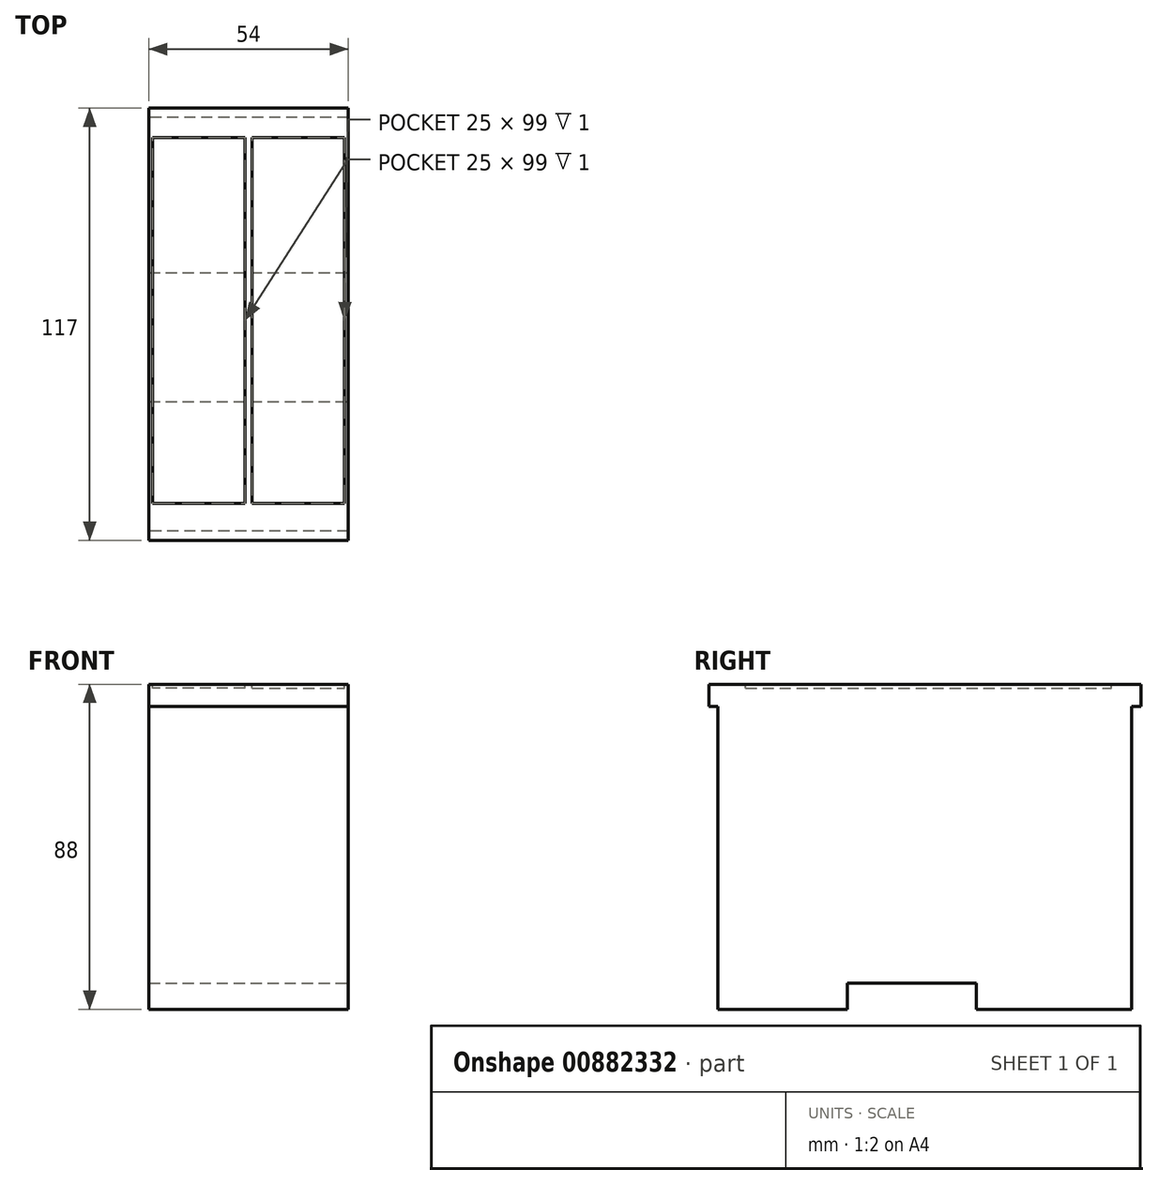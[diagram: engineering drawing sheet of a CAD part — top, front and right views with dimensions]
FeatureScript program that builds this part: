
annotation { "Feature Type Name" : "Feature", "Feature Type Description" : "" }
export const myFeature = defineFeature(function(context is Context, id is Id, definition is map)
    precondition{}
    {
        {
            var Q0;
            Q0=qCreatedBy(makeId("Top.planeOp"),FACE);
            var sketch = newSketch(context, id + "F0", { "sketchPlane" : qUnion([Q0])});
            skLineSegment(sketch, "E0.bottom", {"start": v(0, 58.5) * mm, "end": v(-27, 58.5) * mm});
            skLineSegment(sketch, "E0.top", {"start": v(0, -58.5) * mm, "end": v(-27, -58.5) * mm});
            skLineSegment(sketch, "E0.left", {"start": v(0, 58.5) * mm, "end": v(0, -58.5) * mm});
            skLineSegment(sketch, "E0.right", {"start": v(-27, 58.5) * mm, "end": v(-27, -58.5) * mm});
            skLineSegment(sketch, "E1.bottom", {"start": v(0, 58.5) * mm, "end": v(27, 58.5) * mm});
            skLineSegment(sketch, "E1.top", {"start": v(0, -58.5) * mm, "end": v(27, -58.5) * mm});
            skLineSegment(sketch, "E1.right", {"start": v(27, 58.5) * mm, "end": v(27, -58.5) * mm});
            skLineSegment(sketch, "E2.bottom", {"start": v(1, -48.5) * mm, "end": v(26, -48.5) * mm});
            skLineSegment(sketch, "E2.top", {"start": v(1, 50.5) * mm, "end": v(26, 50.5) * mm});
            skLineSegment(sketch, "E2.left", {"start": v(1, -48.5) * mm, "end": v(1, 50.5) * mm});
            skLineSegment(sketch, "E2.right", {"start": v(26, -48.5) * mm, "end": v(26, 50.5) * mm});
            skPoint(sketch, "E3", {"position": v(13.5, -48.5) * mm});
            skPoint(sketch, "E4", {"position": v(13.5, -58.5) * mm});
            skLineSegment(sketch, "E5.MirrorCS", {"start": v(-1, 50.5) * mm, "end": v(-26, 50.5) * mm});
            skLineSegment(sketch, "E6.MirrorCS", {"start": v(-1, -48.5) * mm, "end": v(-1, 50.5) * mm});
            skLineSegment(sketch, "E7.MirrorCS", {"start": v(-1, -48.5) * mm, "end": v(-26, -48.5) * mm});
            skLineSegment(sketch, "E8.MirrorCS", {"start": v(-26, -48.5) * mm, "end": v(-26, 50.5) * mm});
            skSolve(sketch);
        }
        {
            var Q0;
            Q0 = qSketchRegion(id + "F0", true);
            var Q1;
            Q1=makeQuery(id+"F0.imprint","IMPRINT",FACE,{"disambiguationData":[TD([[makeQuery(id+"F0.imprint","IMPRINT",EDGE,{"derivedFrom":sQuery(id+"F0.wireOp",EDGE,"E5.MirrorCS")}),1.0]])]});
            var Q2;
            Q2=makeQuery(id+"F0.imprint","IMPRINT",FACE,{"disambiguationData":[TD([[makeQuery(id+"F0.imprint","IMPRINT",EDGE,{"derivedFrom":sQuery(id+"F0.wireOp",EDGE,"E2.bottom")}),1.0]])]});
            extrude(context, id + "F1", {"entities" : qUnion([Q0, Q1, Q2]), "oppositeDirection" : true, "depth" : 88 * mm, "offsetDistance" : 25 * mm});
        }
        {
            var Q0;
            Q0=makeQuery(id+"F0.imprint","IMPRINT",FACE,{"disambiguationData":[TD([[makeQuery(id+"F0.imprint","IMPRINT",EDGE,{"derivedFrom":sQuery(id+"F0.wireOp",EDGE,"E5.MirrorCS")}),1.0]])]});
            var Q1;
            Q1=makeQuery(id+"F0.imprint","IMPRINT",FACE,{"disambiguationData":[TD([[makeQuery(id+"F0.imprint","IMPRINT",EDGE,{"derivedFrom":sQuery(id+"F0.wireOp",EDGE,"E2.bottom")}),1.0]])]});
            extrude(context, id + "F2", {"entities" : qUnion([Q0, Q1]), "operationType" : NewBodyOperationType.REMOVE, "oppositeDirection" : true, "depth" : 1 * mm, "offsetDistance" : 25 * mm});
        }
        {
            var Q0;
            {var subQ0=sQuery(id+"F0.wireOp",EDGE,"E1.top");var subQ1=sQuery(id+"F0.wireOp",EDGE,"E0.top");var subQ2=sQuery(id+"F0.wireOp",EDGE,"E0.right");var subQ3=sQuery(id+"F0.wireOp",EDGE,"E1.right");Q0=makeQuery(id+"FFmhZgsTpmXwhqy_1.boolean.opBoolean","SPLIT",FACE,{"disambiguationData":[TD([makeQuery(id+"FFmhZgsTpmXwhqy_1.opExtrude","SWEPT_FACE",FACE,{"disambiguationData":[OSD([sQuery(id+"F5.wireOp",EDGE,"E11.left")])]})])],"derivedFrom":makeQuery(id+"F1.opExtrude","CAP_FACE",FACE,{"disambiguationData":[OSD([sQuery(id+"F0.wireOp",EDGE,"E0.bottom"),subQ1,subQ2,sQuery(id+"F0.wireOp",EDGE,"E1.bottom"),subQ0,subQ3])],"isStart":false})});}
            var sketch = newSketch(context, id + "F3", { "sketchPlane" : qUnion([Q0])});
            skLineSegment(sketch, "E9.bottom", {"start": v(27, 56) * mm, "end": v(-27, 56) * mm});
            skLineSegment(sketch, "E9.top", {"start": v(27, -56) * mm, "end": v(-27, -56) * mm});
            skLineSegment(sketch, "E9.left", {"start": v(27, 56) * mm, "end": v(27, -56) * mm});
            skLineSegment(sketch, "E9.right", {"start": v(-27, 56) * mm, "end": v(-27, -56) * mm});
            skPoint(sketch, "E9.middle", {"position": v(0, 0) * mm});
            skLineSegment(sketch, "E10.bottom", {"start": v(27, 58.5) * mm, "end": v(-27, 58.5) * mm});
            skLineSegment(sketch, "E10.top", {"start": v(27, -58.5) * mm, "end": v(-27, -58.5) * mm});
            skLineSegment(sketch, "E10.left", {"start": v(27, 58.5) * mm, "end": v(27, -58.5) * mm});
            skLineSegment(sketch, "E10.right", {"start": v(-27, 58.5) * mm, "end": v(-27, -58.5) * mm});
            skSolve(sketch);
        }
        {
            var Q0;
            {var subQ0=sQuery(id+"F3.wireOp",EDGE,"E9.bottom");Q0=makeQuery(id+"F3.imprint","IMPRINT",FACE,{"disambiguationData":[TD([[makeQuery(id+"F3.imprint","IMPRINT",EDGE,{"derivedFrom":subQ0}),-1.0]])]});}
            var Q1;
            {var subQ0=sQuery(id+"F3.wireOp",EDGE,"E9.top");Q1=makeQuery(id+"F3.imprint","IMPRINT",FACE,{"disambiguationData":[TD([[makeQuery(id+"F3.imprint","IMPRINT",EDGE,{"derivedFrom":subQ0}),1.0]])]});}
            extrude(context, id + "F4", {"entities" : qUnion([Q0, Q1]), "operationType" : NewBodyOperationType.REMOVE, "oppositeDirection" : true, "depth" : 82 * mm, "offsetDistance" : 25 * mm});
        }
        {
            var Q0;
            Q0=makeQuery(id+"F1.opExtrude","SWEPT_FACE",FACE,{"disambiguationData":[OSD([sQuery(id+"F0.wireOp",EDGE,"E1.right")])]});
            var sketch = newSketch(context, id + "F5", { "sketchPlane" : qUnion([Q0])});
            skLineSegment(sketch, "E11.bottom", {"start": v(-21, -88) * mm, "end": v(14, -88) * mm});
            skLineSegment(sketch, "E11.top", {"start": v(-21, -81) * mm, "end": v(14, -81) * mm});
            skLineSegment(sketch, "E11.left", {"start": v(-21, -88) * mm, "end": v(-21, -81) * mm});
            skLineSegment(sketch, "E11.right", {"start": v(14, -88) * mm, "end": v(14, -81) * mm});
            skSolve(sketch);
        }
        {
            var Q0;
            Q0=makeQuery(id+"F5.imprint","IMPRINT",FACE,{"disambiguationData":[TD([[makeQuery(id+"F5.imprint","IMPRINT",EDGE,{"derivedFrom":sQuery(id+"F5.wireOp",EDGE,"E11.bottom")}),-1.0]])]});
            extrude(context, id + "F6", {"entities" : qUnion([Q0]), "operationType" : NewBodyOperationType.REMOVE, "endBound" : BoundingType.UP_TO_NEXT, "oppositeDirection" : true, "depth" : 25 * mm, "offsetDistance" : 25 * mm});
        }
    });
